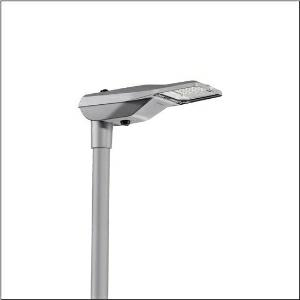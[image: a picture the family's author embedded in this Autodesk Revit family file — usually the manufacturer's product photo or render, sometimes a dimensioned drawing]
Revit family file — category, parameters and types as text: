
# Revit family: streetlight_sl_21_iq_micro___st1_5a_5xe1p31y08cb_38f8
name_source: partatom
category: Lighting Fixtures
units: mm (PartAtom-declared; Revit-internal decimal feet)

## family parameters
Cut with Voids When Loaded = No
Host = Face
Light Source = No
Part Type = Normal
Room Calculation Point = No
Round Connector Dimension = Use Diameter
Shared = No

## types (1)
- --- (1 x LED, 2840 lm, 19.1 W, 3000K)
    Apparent Load = 19 VA
    CIE Flux Codes = 22 53 95 100 100
    Color Rendering = 70
    Color Temperature = 3000K
    Default Elevation = 1800 mm
    Description = Streetlight SL 21 iQ micro, mast luminaire, primary light control with lens, of PMMA, primary optical cover: cover, of toughened safety glass, transparent, light distribution: ST1.5a, light emission: direct distribution, primary light characteristic: asymmetric, installation type: post-top, side-entry, LED, High Power LED, rated luminous flux: 2.840lm, luminous efficacy: 149lm/W, light colour: 730, colour temperature: 3000K, control gear: iQ-Street Remote, D4i with power reduction, control: pre-setting: logarithmic dimming characteristic, Street-Remote, Auto-Match, Temp-Guard, Lumen-Switch, Night-Set, Smart-Wire, Light-Fading, Desk-Remote (wireless, voltage-free reading and setting of iQ features in the workshop via application-optimized NFC function/RFID function), optimised constant luminous flux control (CLO 2.0), mains connection: 220..240V, AC, 50/60Hz, start of lifetime: 19W, end of service life: 20W, reduction: 9W, luminaire housing, of diecast aluminium, powder-coated, Siteco® metallic grey (DB 702S), corrosivity category C5 mid according to DIN EN ISO 12944, please order mast flange separately, inclination adjustable: 0°, 5°, 10°, 15°, sealing non-destructively replaceable, multi-level sealing system, length: 528mm, width: 235mm, height: 110mm, mast flange for spigot size: 42mm (side-entry): 5XC10008XM4, 60/48mm (side-entry/post-top): 5XC10108XM2, 76/60mm (side-entry/post-top): 5XC10108XM1, mounting height: 4..8m, Smart Interface below and above, protection rating (complete): IP66, insulation class (complete): insulation class II (safety insulation), certification: CE, ENEC, ENEC+, VDE, impact resistance: IK10, permissible operating ambient temperature for outdoor applications: -40..+50°C, standard-compliant lighting for roads and squares, packaging unit: 1 piece

Light Distribution: ST1.5a
    Height = 110 mm
    Lamp = 1 x LED
    Lamp Light Flux = 2840 lm
    Lamp Power = 19.1 W
    Lamp count = 1
    Length = 528 mm
    Luminous efficacy = 149 lm/W
    Manufacturer = Siteco
    ModVariant = No
    Model = 5XE1P31Y08CB
    Number of Poles = 1
    OnlyDefault = Yes
    Power Factor = 1
    Product Name = Streetlight SL 21 iQ micro | ST1.5a
    Product group = mast luminaire | pylon top
    ProductGroupID = 6100
    Protection Class = Protection class II
    Protection Degree = IP 66
    RLX_Detail_Level = 1
    RLX_Emergency_Light_Flux = 0 lm
    RLX_Emergency_Type = 0
    RLX_Emergency_Type_DB = No
    RlxData = <blob elided: 102177 chars, md5=62f8671b>
    Socket = socket
    Standby Power = 0 W
    System Light Flux = 2840 lm
    System Power = 19 W
    Type Comments = factory setting: luminous flux: 100 % | dim-lin: 254 | 387 mA
    Type Image = l_1007239.jpg
    URL = http://relux.com
    VarID = @adj_133497
    Voltage = 0 V
    Weight = 0.00 kg
    Width = 235 mm

## geometry (parser evidence)
native form markers: Blend x4, Sweep x10
no freeform markers — native parametric forms only
